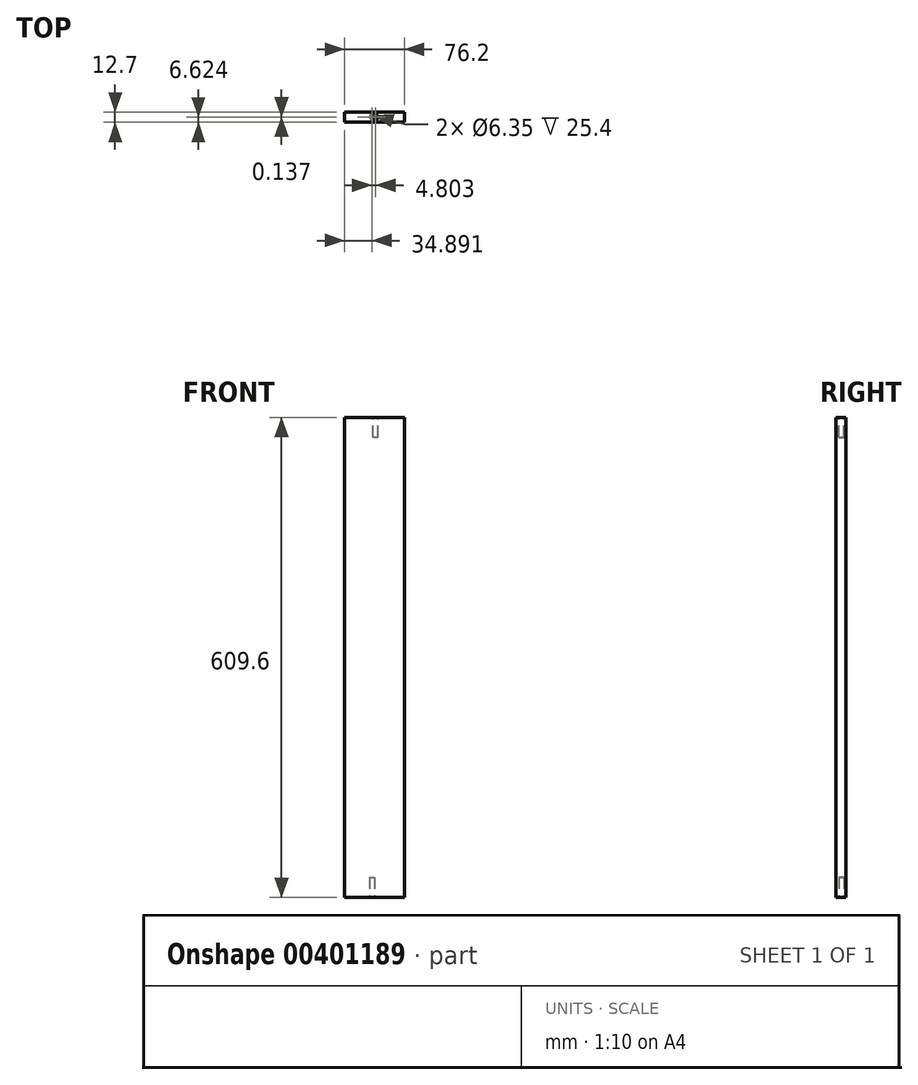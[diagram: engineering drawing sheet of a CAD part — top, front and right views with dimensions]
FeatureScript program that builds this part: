
annotation { "Feature Type Name" : "Feature", "Feature Type Description" : "" }
export const myFeature = defineFeature(function(context is Context, id is Id, definition is map)
    precondition{}
    {
        {
            var Q0;
            Q0=qCreatedBy(makeId("Front.planeOp"),FACE);
            var sketch = newSketch(context, id + "F0", { "sketchPlane" : qUnion([Q0])});
            skLineSegment(sketch, "E0.bottom", {"start": v(0, 0) * mm, "end": v(-76.2, 0) * mm});
            skLineSegment(sketch, "E0.top", {"start": v(0, 609.6) * mm, "end": v(-76.2, 609.6) * mm});
            skLineSegment(sketch, "E0.left", {"start": v(0, 0) * mm, "end": v(0, 609.6) * mm});
            skLineSegment(sketch, "E0.right", {"start": v(-76.2, 0) * mm, "end": v(-76.2, 609.6) * mm});
            skSolve(sketch);
        }
        {
            var Q0;
            Q0 = qSketchRegion(id + "F0", true);
            extrude(context, id + "F1", {"entities" : qUnion([Q0]), "depth" : 12.7 * mm});
        }
        {
            var Q0;
            Q0=makeQuery(id+"F1.opExtrude","SWEPT_FACE",FACE,{"disambiguationData":[OSD([sQuery(id+"F0.wireOp",EDGE,"E0.bottom")])]});
            var sketch = newSketch(context, id + "F2", { "sketchPlane" : qUnion([Q0])});
            skCircle(sketch, "E1", {"center": v(-41.3, 5.94) * mm, "radius": 3.18 * mm});
            skSolve(sketch);
        }
        {
            var Q0;
            Q0 = qSketchRegion(id + "F2", true);
            extrude(context, id + "F3", {"entities" : qUnion([Q0]), "operationType" : NewBodyOperationType.REMOVE, "oppositeDirection" : true, "depth" : 25.4 * mm});
        }
        {
            var Q0;
            Q0=makeQuery(id+"F1.opExtrude","SWEPT_FACE",FACE,{"disambiguationData":[OSD([sQuery(id+"F0.wireOp",EDGE,"E0.top")])]});
            var sketch = newSketch(context, id + "F4", { "sketchPlane" : qUnion([Q0])});
            skCircle(sketch, "E2", {"center": v(-36.5, -6.08) * mm, "radius": 3.17 * mm});
            skSolve(sketch);
        }
        {
            var Q0;
            Q0 = qSketchRegion(id + "F4", true);
            extrude(context, id + "F5", {"entities" : qUnion([Q0]), "operationType" : NewBodyOperationType.REMOVE, "oppositeDirection" : true, "depth" : 25.4 * mm});
        }
    });
